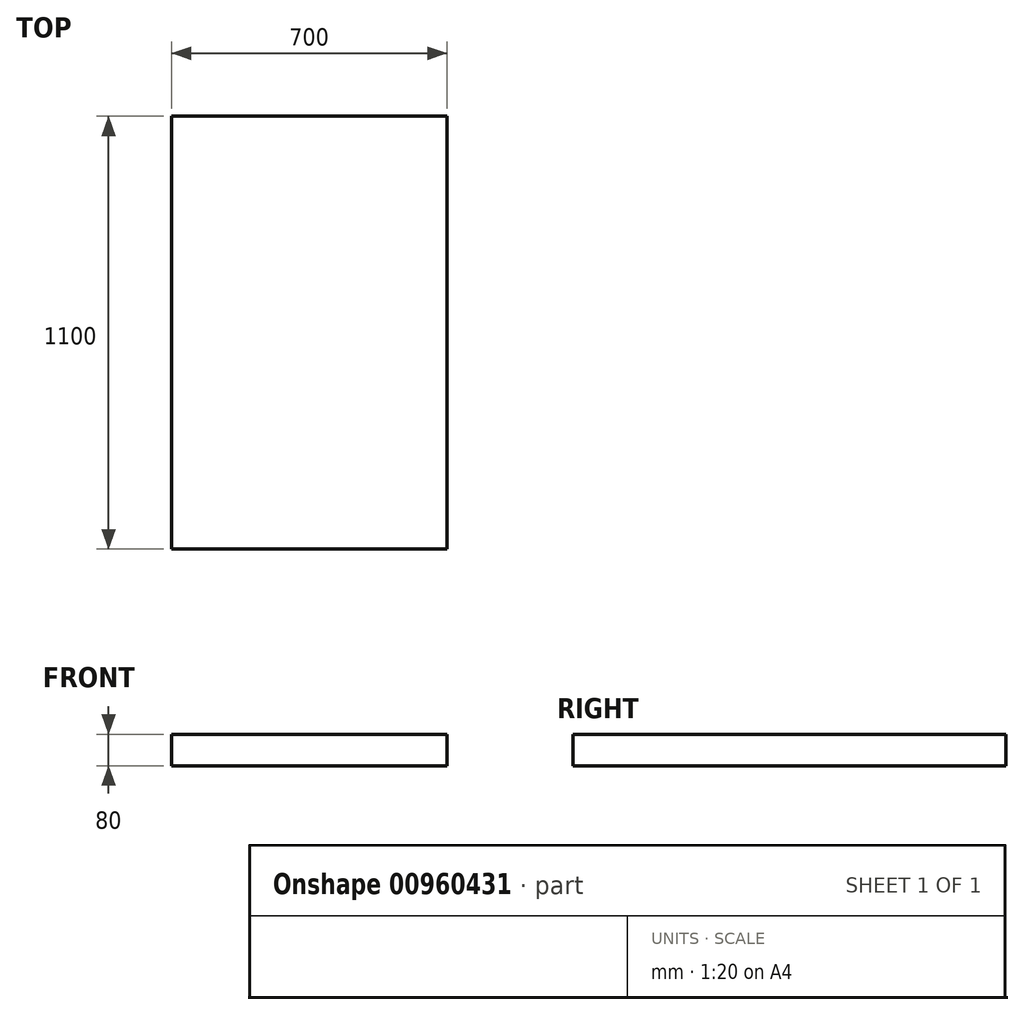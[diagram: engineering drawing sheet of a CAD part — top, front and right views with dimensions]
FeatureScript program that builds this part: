
annotation { "Feature Type Name" : "Feature", "Feature Type Description" : "" }
export const myFeature = defineFeature(function(context is Context, id is Id, definition is map)
    precondition{}
    {
        {
            var Q0;
            Q0=qCreatedBy(makeId("Top.planeOp"),FACE);
            var sketch = newSketch(context, id + "F0", { "sketchPlane" : qUnion([Q0])});
            skLineSegment(sketch, "E0.bottom", {"start": v(350, -550) * mm, "end": v(-350, -550) * mm});
            skLineSegment(sketch, "E0.top", {"start": v(350, 550) * mm, "end": v(-350, 550) * mm});
            skLineSegment(sketch, "E0.left", {"start": v(350, -550) * mm, "end": v(350, 550) * mm});
            skLineSegment(sketch, "E0.right", {"start": v(-350, -550) * mm, "end": v(-350, 550) * mm});
            skPoint(sketch, "E0.middle", {"position": v(0, 0) * mm});
            skSolve(sketch);
        }
        {
            var Q0;
            Q0 = qSketchRegion(id + "F0", true);
            extrude(context, id + "F1", {"entities" : qUnion([Q0]), "depth" : 80 * mm, "offsetDistance" : 25 * mm});
        }
    });
